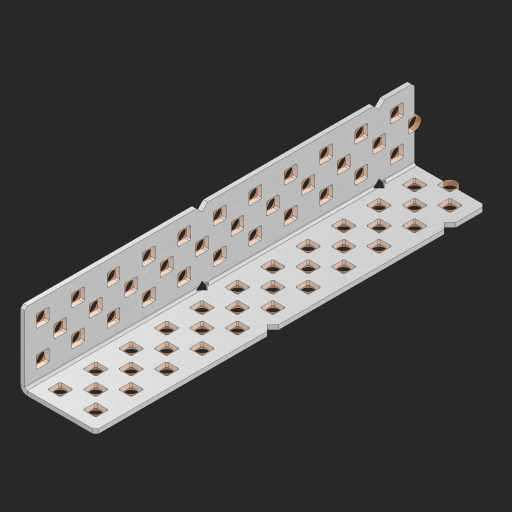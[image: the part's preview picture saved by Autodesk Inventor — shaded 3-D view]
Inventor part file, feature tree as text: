
AUTODESK INVENTOR PART (.ipt)
format: ipt  version: 2023 (Build 270158000, 158)  size: 1,077,248 bytes
history: native  units: in
note: dims shown in document units (in); Inventor stores cm internally (conversion verified against a paired STEP export)
features: other x72, extrude x64, sheet_metal_op x8, sketch x7, pattern_linear x2, mirror x1, chamfer x1
ambient origin geometry x8: Origin, YZ Plane, XZ Plane, XY Plane, X Axis, Y Axis, Z Axis, Center Point
bodies: Solid1 (feature_tree), Body (feature_tree)
feature tree (155):
  sheet_metal_op  "Flanges"
  sheet_metal_op  "Body Pattern"
  pattern_linear  "Center Pattern"  Spacing1=1.0in  [1 undecoded]
  other  "Arc Length"
  pattern_linear  "Notch Pattern"  Spacing1=0.25in  [1 undecoded]
  other  "Diagonal Plane"
  mirror  "Everything Mirrored"
  chamfer  "End Chamfer"
  sketch  "Sketch1"  dims[d0=1.0in]
  other  "Plate1"
  sketch  "Sketch2"  dims[d1=5.5in]
  other  "Plate2"
  sheet_metal_op  "Bend1"
  sheet_metal_op  "Corner1"
  sketch  "Sketch8"  dims[d2=0.0625in]
  sketch  "Sketch9"  dims[d3=0.0625in]
  other  "Srf91"
  sheet_metal_op  "Body Pattern Sketch"
  other  "Srf92"
  sketch  "Sketch13"  dims[d4=0.0312in]
  sketch  "Sketch15"  dims[d5=0.125in]
  sketch  "Sketch16"  dims[d6=0.0625in d7=1.0in d8=90.0deg d9=0.0312in d10=0.25in d11=0.0625in d12=0.0625in d49=0.182in d50=0.02in d52=0.25in d53=0.0625in d54=0.0in d55=0.172in d56=1.0in d57=0.0in d60=4.3307in d62=0.5in d63=0.7874in d65=0.5in d85=0.1473in d86=0.1782in d89=0.0625in d90=0.0in d91=0.04in d92=0.0491in d95=2.5in d96=0.04in d97=0.25in d98=45.0deg d99=0.25in d106=0.182in d107=0.02in d108=0.5in d110=0.0625in d111=0.0in d112=0.172in d113=0.5in d114=0.0in d117=0.5in d123=0.25in d125=0.25in d126=0.0491in d127=0.1473in d128=0.08in d129=0.04in d130=2.5in]
  other  "Srf786"
  other  "Srf856"
  other  "Srf857"
  other  "Srf858"
  other  "Srf859"
  other  "Srf860"
  other  "Srf861"
  other  "Srf889"
  other  "Srf890"
  other  "Srf891"
  other  "Srf1275"
  other  "Srf1276"
  other  "Srf1278"
  other  "Srf1279"
  other  "Srf1280"
  other  "Srf1281"
  other  "Srf1282"
  other  "Srf1283"
  other  "Srf1277"
  other  "Srf1285"
  other  "Srf1286"
  other  "Srf1287"
  other  "Srf1383"
  other  "Srf1384"
  other  "Srf1385"
  other  "Srf1386"
  other  "Srf1387"
  other  "Srf1388"
  other  "Srf1389"
  other  "Srf1390"
  other  "Srf1391"
  other  "Srf1392"
  other  "Srf1393"
  other  "Srf1394"
  other  "Srf1395"
  other  "Srf1396"
  other  "Srf1445"
  other  "Srf1446"
  other  "Srf1447"
  other  "Srf1448"
  other  "Srf1449"
  other  "Srf1450"
  other  "Srf1451"
  other  "Srf1475"
  other  "Srf1476"
  other  "Srf1477"
  other  "Srf1478"
  other  "Srf1479"
  other  "Srf1480"
  other  "Srf1481"
  other  "Srf1482"
  other  "Srf1483"
  other  "Srf1484"
  other  "Srf1485"
  other  "Srf1486"
  other  "Srf1487"
  other  "Srf1488"
  other  "Srf1537"
  other  "Srf1538"
  other  "Srf1539"
  other  "Srf1540"
  other  "Srf1541"
  other  "Srf1542"
  other  "Srf1543"
  sheet_metal_op  "Body Stamp"
  sheet_metal_op  "Body Circle"
  other  "Center Stamp"
  other  "Center Circle"
  sheet_metal_op  "Notch"
  extrude  "ExtrusionSrf92"  Depth=0.0625in
  extrude  "ExtrusionSrf856"  Depth=0.0625in
  extrude  "ExtrusionSrf857"  Depth=0.182in
  extrude  "ExtrusionSrf858"  Depth=0.02in
  extrude  "ExtrusionSrf859"  Depth=0.25in
  extrude  "ExtrusionSrf860"  Depth=0.0625in
  extrude  "ExtrusionSrf861"  TaperAngle=0.0deg  [1 undecoded]
  extrude  "ExtrusionSrf889"  Depth=2.5in
  extrude  "ExtrusionSrf890"  Depth=1.0in TaperAngle=0.0deg
  extrude  "ExtrusionSrf891"  Depth=2.5in
  extrude  "ExtrusionSrf1275"  Depth=0.5in
  extrude  "ExtrusionSrf1276"  Depth=2.5in
  extrude  "ExtrusionSrf1277"  Depth=2.5in
  extrude  "ExtrusionSrf1278"  Depth=0.0625in
  extrude  "ExtrusionSrf1279"  Depth=2.5in TaperAngle=0.0deg
  extrude  "ExtrusionSrf1280"  Depth=2.5in
  extrude  "ExtrusionSrf1281"  Depth=0.25in TaperAngle=45.0deg
  extrude  "ExtrusionSrf1282"  Depth=0.25in
  extrude  "ExtrusionSrf1345"  Depth=0.182in
  extrude  "ExtrusionSrf1346"  Depth=0.02in
  extrude  "ExtrusionSrf1347"  Depth=0.5in
  extrude  "ExtrusionSrf1348"  Depth=0.0625in
  extrude  "ExtrusionSrf1383"  TaperAngle=0.0deg  [1 undecoded]
  extrude  "ExtrusionSrf1384"  Depth=2.5in
  extrude  "ExtrusionSrf1385"  Depth=0.5in TaperAngle=0.0deg
  extrude  "ExtrusionSrf1386"  Depth=0.5in
  extrude  "ExtrusionSrf1387"  Depth=0.25in
  extrude  "ExtrusionSrf1388"  Depth=0.25in
  extrude  "ExtrusionSrf1389"  Depth=2.5in
  extrude  "ExtrusionSrf1390"  Depth=2.5in
  extrude  "ExtrusionSrf1391"  Depth=2.5in
  extrude  "ExtrusionSrf1392"  Depth=2.5in
  extrude  "ExtrusionSrf1393"  Depth=2.5in
  extrude  "ExtrusionSrf1394"  [1 undecoded]
  extrude  "ExtrusionSrf1395"  [1 undecoded]
  extrude  "ExtrusionSrf1396"  [1 undecoded]
  extrude  "ExtrusionSrf1445"  [1 undecoded]
  extrude  "ExtrusionSrf1446"  [1 undecoded]
  extrude  "ExtrusionSrf1447"  [1 undecoded]
  extrude  "ExtrusionSrf1448"  [1 undecoded]
  extrude  "ExtrusionSrf1449"  [1 undecoded]
  extrude  "ExtrusionSrf1450"  [1 undecoded]
  extrude  "ExtrusionSrf1451"  [1 undecoded]
  extrude  "ExtrusionSrf1475"  [1 undecoded]
  extrude  "ExtrusionSrf1476"  [1 undecoded]
  extrude  "ExtrusionSrf1477"  [1 undecoded]
  extrude  "ExtrusionSrf1478"  [1 undecoded]
  extrude  "ExtrusionSrf1479"  [1 undecoded]
  extrude  "ExtrusionSrf1480"  [1 undecoded]
  extrude  "ExtrusionSrf1481"  [1 undecoded]
  extrude  "ExtrusionSrf1482"  [1 undecoded]
  extrude  "ExtrusionSrf1483"  [1 undecoded]
  extrude  "ExtrusionSrf1484"  [1 undecoded]
  extrude  "ExtrusionSrf1485"  [1 undecoded]
  extrude  "ExtrusionSrf1486"  [1 undecoded]
  extrude  "ExtrusionSrf1487"  [1 undecoded]
  extrude  "ExtrusionSrf1488"  [1 undecoded]
  extrude  "ExtrusionSrf1537"  [1 undecoded]
  extrude  "ExtrusionSrf1538"  [1 undecoded]
  extrude  "ExtrusionSrf1539"  [1 undecoded]
  extrude  "ExtrusionSrf1540"  [1 undecoded]
  extrude  "ExtrusionSrf1541"  [1 undecoded]
  extrude  "ExtrusionSrf1542"  [1 undecoded]
  extrude  "ExtrusionSrf1543"  [1 undecoded]
note: 35 required parameter values undecoded (feature->parameter linkage not recoverable at this tier; creation-order binding heuristic only, values carry confidence <= 0.55)
